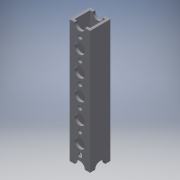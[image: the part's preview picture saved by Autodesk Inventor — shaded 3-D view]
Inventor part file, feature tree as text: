
AUTODESK INVENTOR PART (.ipt)
format: ipt  version: 2016 (Build 200138000, 138)  size: 229,376 bytes
history: native  units: mm
features: reference x24, sketch x8, hole x6, extrude x2
ambient origin geometry x8: Origin, YZ Plane, XZ Plane, XY Plane, X Axis, Y Axis, Z Axis, Center Point
bodies: Solid1 (feature_tree)
feature tree (40):
  extrude  "Extrusion1"  Depth=16.0mm
  extrude  "Extrusion2"  Depth=12.0mm
  hole  "Hole7"  [1 undecoded]
  hole  "Hole8"  [1 undecoded]
  hole  "Hole9"  [1 undecoded]
  hole  "Hole10"  [1 undecoded]
  hole  "Hole11"  [1 undecoded]
  hole  "Hole12"  [1 undecoded]
  sketch  "Sketch1"  dims[d0=16.0mm d1=16.0mm]
  sketch  "Sketch2"  dims[d2=96.0mm d3=0.0mm d4=12.0mm]
  sketch  "Sketch9"  dims[d5=12.0mm d6=96.0mm d7=0.0mm]
  sketch  "Sketch10"  dims[d52=8.0mm]
  sketch  "Sketch11"  dims[d53=8.0mm d54=6.0mm d55=4.0mm d56=2.0mm d57=90.0deg d58=8.0mm d59=20.594885mm d60=8.0mm]
  reference  "Reference31"
  reference  "Reference32"
  reference  "Reference33"
  reference  "Reference34"
  reference  "Reference35"
  reference  "Reference36"
  sketch  "Sketch12"  dims[d61=8.0mm d62=6.0mm d63=4.0mm d64=2.0mm d65=90.0deg d66=8.0mm d67=20.594885mm]
  reference  "Reference37"
  reference  "Reference38"
  reference  "Reference39"
  reference  "Reference40"
  reference  "Reference41"
  reference  "Reference42"
  sketch  "Sketch13"  dims[d68=3.7mm d69=6.0mm d70=4.0mm d71=2.0mm d72=90.0deg d73=8.0mm d74=20.594885mm]
  reference  "Reference43"
  reference  "Reference44"
  reference  "Reference45"
  reference  "Reference46"
  reference  "Reference47"
  reference  "Reference48"
  sketch  "Sketch14"  dims[d75=8.0mm d76=6.0mm d77=4.0mm d78=2.0mm d79=90.0deg d80=8.0mm d81=20.594885mm d82=3.7mm d83=6.0mm d84=4.0mm d85=2.0mm d86=90.0deg d87=8.0mm d88=20.594885mm d89=8.0mm d90=6.0mm d91=4.0mm d92=2.0mm d93=90.0deg d94=8.0mm d95=20.594885mm]
  reference  "Reference49"
  reference  "Reference50"
  reference  "Reference51"
  reference  "Reference52"
  reference  "Reference53"
  reference  "Reference54"
note: 6 required parameter values undecoded (feature->parameter linkage not recoverable at this tier; creation-order binding heuristic only, values carry confidence <= 0.55)
